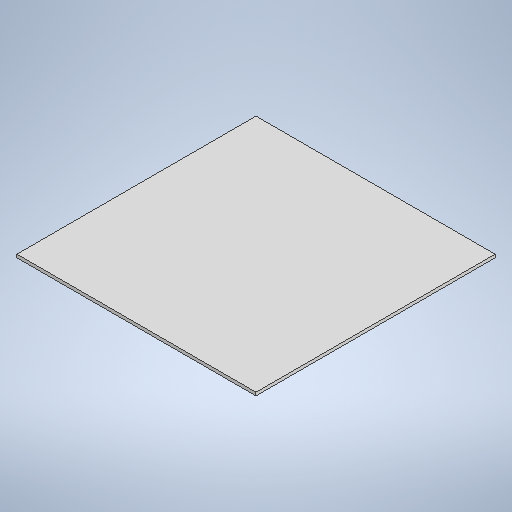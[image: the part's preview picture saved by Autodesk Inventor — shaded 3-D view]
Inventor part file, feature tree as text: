
AUTODESK INVENTOR PART (.ipt)
format: ipt  version: 2025 (Build 290162010, 162A)  size: 258,560 bytes
history: native  units: in
note: dims shown in document units (in); Inventor stores cm internally (conversion verified against a paired STEP export)
features: extrude x1, sketch x1
ambient origin geometry x8: Origin, YZ Plane, XZ Plane, XY Plane, X Axis, Y Axis, Z Axis, Center Point
bodies: Solid1 (feature_tree)
feature tree (2):
  extrude  "Extrusion1"  Depth=300.0in
  sketch  "Sketch1"  dims[d2=300.0in d3=300.0in d4=4.0in d5=0.0in]
